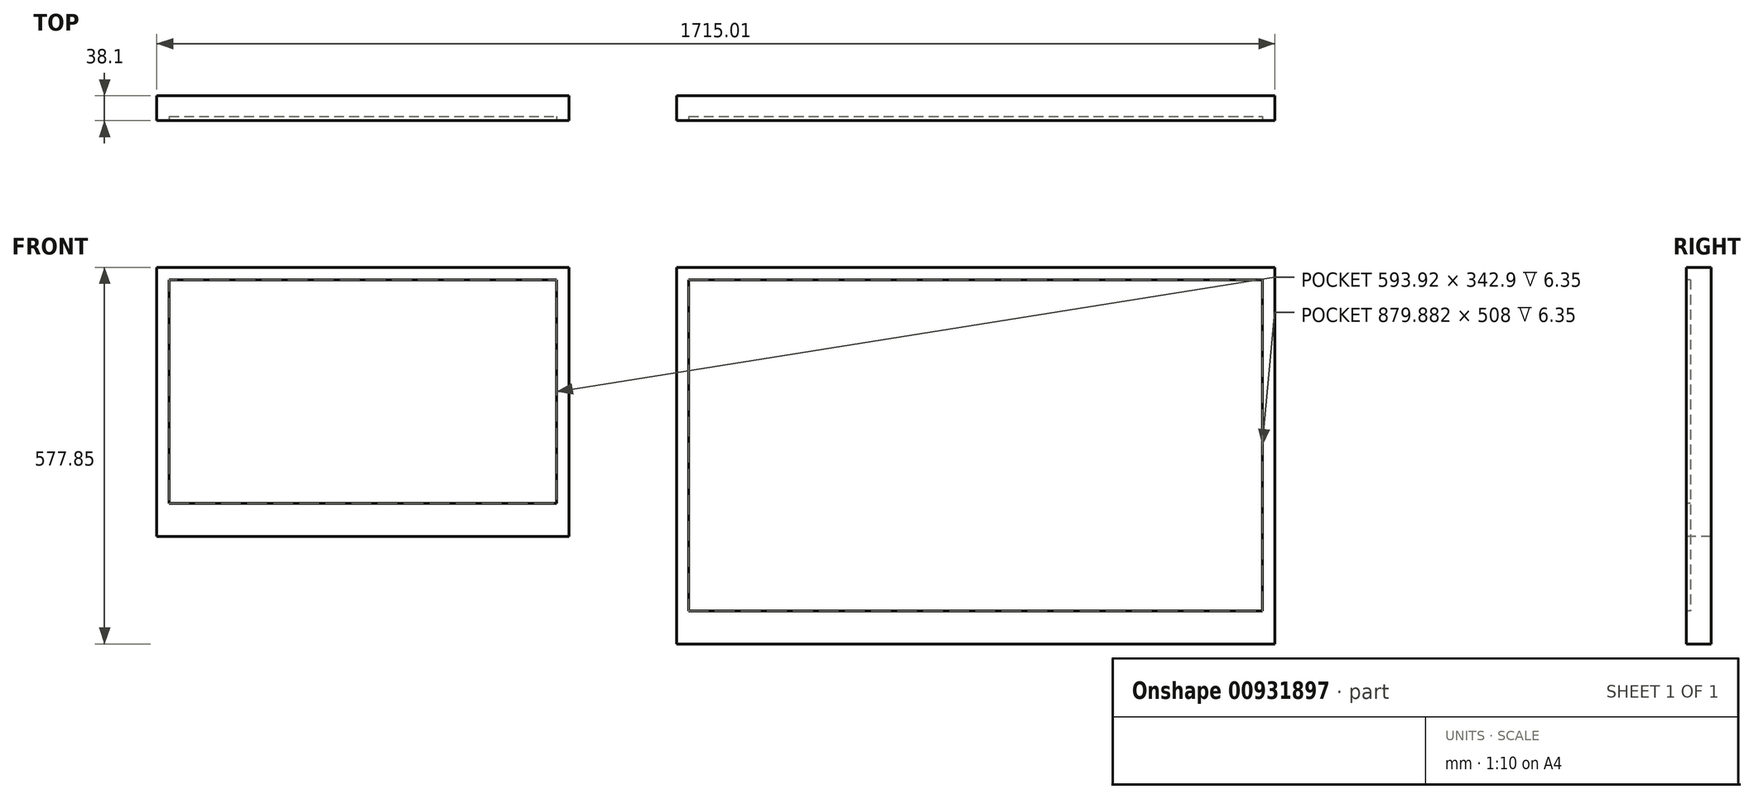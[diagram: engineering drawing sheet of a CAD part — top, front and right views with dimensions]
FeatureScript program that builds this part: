
annotation { "Feature Type Name" : "Feature", "Feature Type Description" : "" }
export const myFeature = defineFeature(function(context is Context, id is Id, definition is map)
    precondition{}
    {
        {
            var Q0;
            Q0=qCreatedBy(makeId("Front.planeOp"),FACE);
            var sketch = newSketch(context, id + "F0", { "sketchPlane" : qUnion([Q0])});
            skLineSegment(sketch, "E0.bottom", {"start": v(0, 0) * mm, "end": v(593.92, 0) * mm});
            skLineSegment(sketch, "E0.top", {"start": v(0, -342.9) * mm, "end": v(593.92, -342.9) * mm});
            skLineSegment(sketch, "E0.left", {"start": v(0, 0) * mm, "end": v(0, -342.9) * mm});
            skLineSegment(sketch, "E0.right", {"start": v(593.92, 0) * mm, "end": v(593.92, -342.9) * mm});
            skLineSegment(sketch, "E1.bottom", {"start": v(797.03, 0) * mm, "end": v(1676.9, 0) * mm});
            skLineSegment(sketch, "E1.top", {"start": v(797.03, -508) * mm, "end": v(1676.9, -508) * mm});
            skLineSegment(sketch, "E1.left", {"start": v(797.03, 0) * mm, "end": v(797.03, -508) * mm});
            skLineSegment(sketch, "E1.right", {"start": v(1676.9, 0) * mm, "end": v(1676.9, -508) * mm});
            skLineSegment(sketch, "E2.0", {"start": v(-19.05, 19.05) * mm, "end": v(612.97, 19.05) * mm});
            skLineSegment(sketch, "E2.1", {"start": v(-19.05, 19.05) * mm, "end": v(-19.05, -393.7) * mm});
            skLineSegment(sketch, "E2.3", {"start": v(612.97, 19.05) * mm, "end": v(612.97, -393.7) * mm});
            skLineSegment(sketch, "E3.0", {"start": v(777.98, 19.05) * mm, "end": v(1695.96, 19.05) * mm});
            skLineSegment(sketch, "E3.1", {"start": v(777.98, 19.05) * mm, "end": v(777.98, -558.8) * mm});
            skLineSegment(sketch, "E3.3", {"start": v(1695.96, 19.05) * mm, "end": v(1695.96, -558.8) * mm});
            skLineSegment(sketch, "E4", {"start": v(-19.05, -393.7) * mm, "end": v(612.97, -393.7) * mm});
            skLineSegment(sketch, "E5", {"start": v(777.98, -558.8) * mm, "end": v(1695.96, -558.8) * mm});
            skSolve(sketch);
        }
        {
            var Q0;
            Q0 = qSketchRegion(id + "F0", true);
            extrude(context, id + "F1", {"entities" : qUnion([Q0]), "oppositeDirection" : true, "depth" : 38.1 * mm, "offsetDistance" : 25.4 * mm});
        }
        {
            var Q0;
            Q0=makeQuery(id+"F0.imprint","IMPRINT",FACE,{"disambiguationData":[TD([[makeQuery(id+"F0.imprint","IMPRINT",EDGE,{"derivedFrom":sQuery(id+"F0.wireOp",EDGE,"E0.bottom")}),-1.0]])]});
            var Q1;
            Q1=makeQuery(id+"F0.imprint","IMPRINT",FACE,{"disambiguationData":[TD([[makeQuery(id+"F0.imprint","IMPRINT",EDGE,{"derivedFrom":sQuery(id+"F0.wireOp",EDGE,"E1.bottom")}),-1.0]])]});
            extrude(context, id + "F2", {"entities" : qUnion([Q0, Q1]), "operationType" : NewBodyOperationType.ADD, "oppositeDirection" : true, "depth" : 38.1 * mm, "offsetDistance" : 25.4 * mm});
        }
        {
            var Q0;
            Q0=makeQuery(id+"F0.imprint","IMPRINT",FACE,{"disambiguationData":[TD([[makeQuery(id+"F0.imprint","IMPRINT",EDGE,{"derivedFrom":sQuery(id+"F0.wireOp",EDGE,"E0.bottom")}),-1.0]])]});
            var Q1;
            Q1=makeQuery(id+"F0.imprint","IMPRINT",FACE,{"disambiguationData":[TD([[makeQuery(id+"F0.imprint","IMPRINT",EDGE,{"derivedFrom":sQuery(id+"F0.wireOp",EDGE,"E1.bottom")}),-1.0]])]});
            extrude(context, id + "F3", {"entities" : qUnion([Q0, Q1]), "operationType" : NewBodyOperationType.REMOVE, "oppositeDirection" : true, "depth" : 6.35 * mm, "offsetDistance" : 25.4 * mm});
        }
    });
